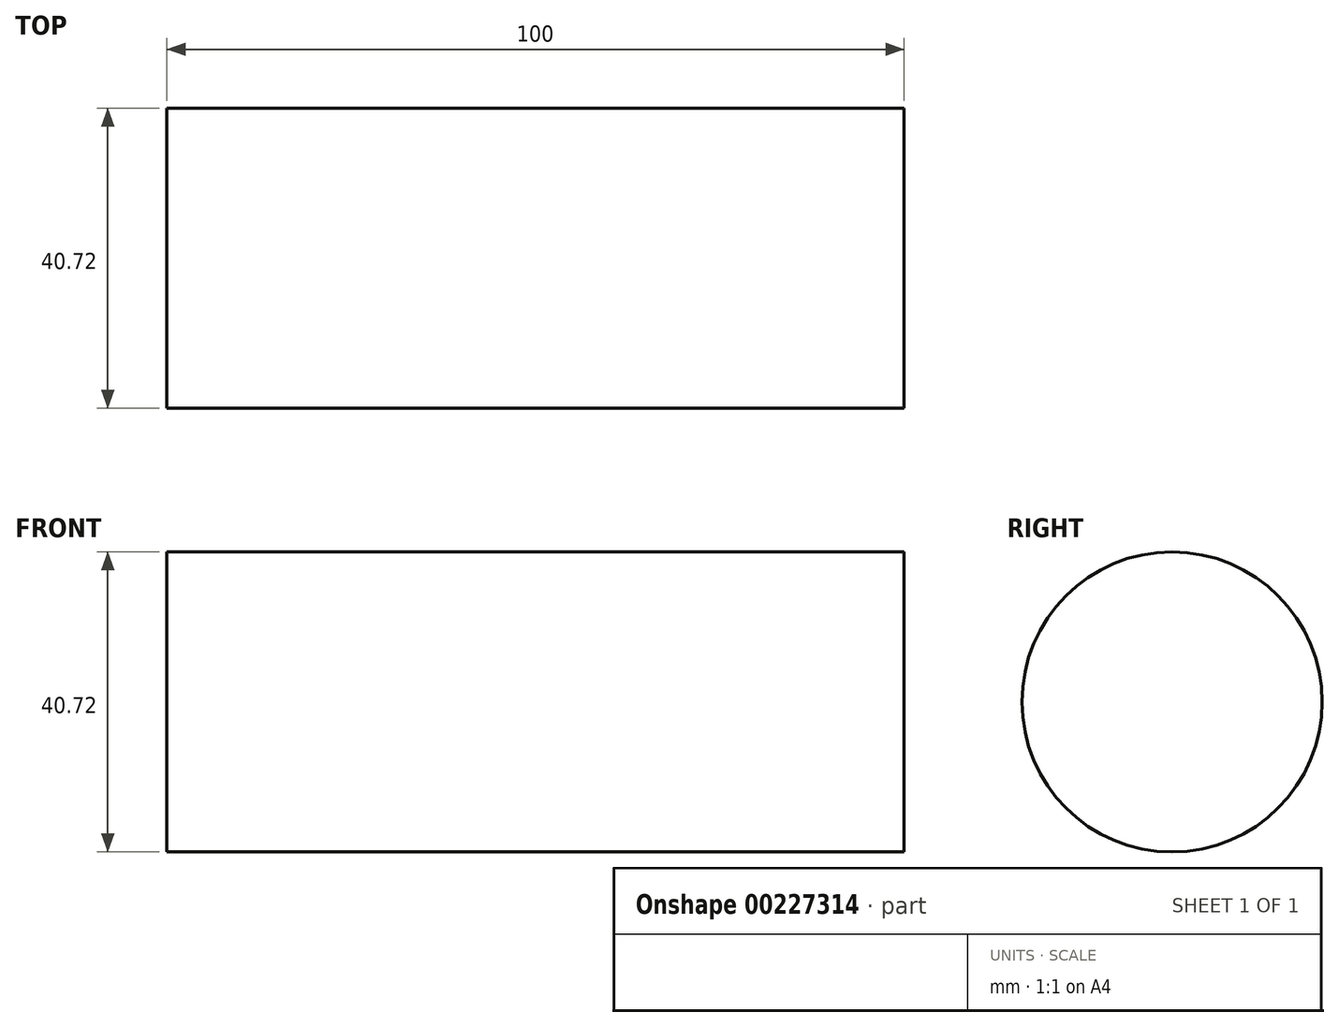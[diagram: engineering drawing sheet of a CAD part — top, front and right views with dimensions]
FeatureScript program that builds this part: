
annotation { "Feature Type Name" : "Feature", "Feature Type Description" : "" }
export const myFeature = defineFeature(function(context is Context, id is Id, definition is map)
    precondition{}
    {
        {
            var Q0;
            Q0=qCreatedBy(makeId("Right.planeOp"),FACE);
            var sketch = newSketch(context, id + "F0", { "sketchPlane" : qUnion([Q0])});
            skCircle(sketch, "E0", {"center": v(0, 0) * mm, "radius": 20.36 * mm});
            skSolve(sketch);
        }
        {
            var Q0;
            Q0=sQuery(id+"F0.wireOp",EDGE,"E0");
            extrude(context, id + "F1", {"bodyType" : ToolBodyType.SURFACE, "surfaceEntities" : qUnion([Q0]), "depth" : 100 * mm});
        }
    });
